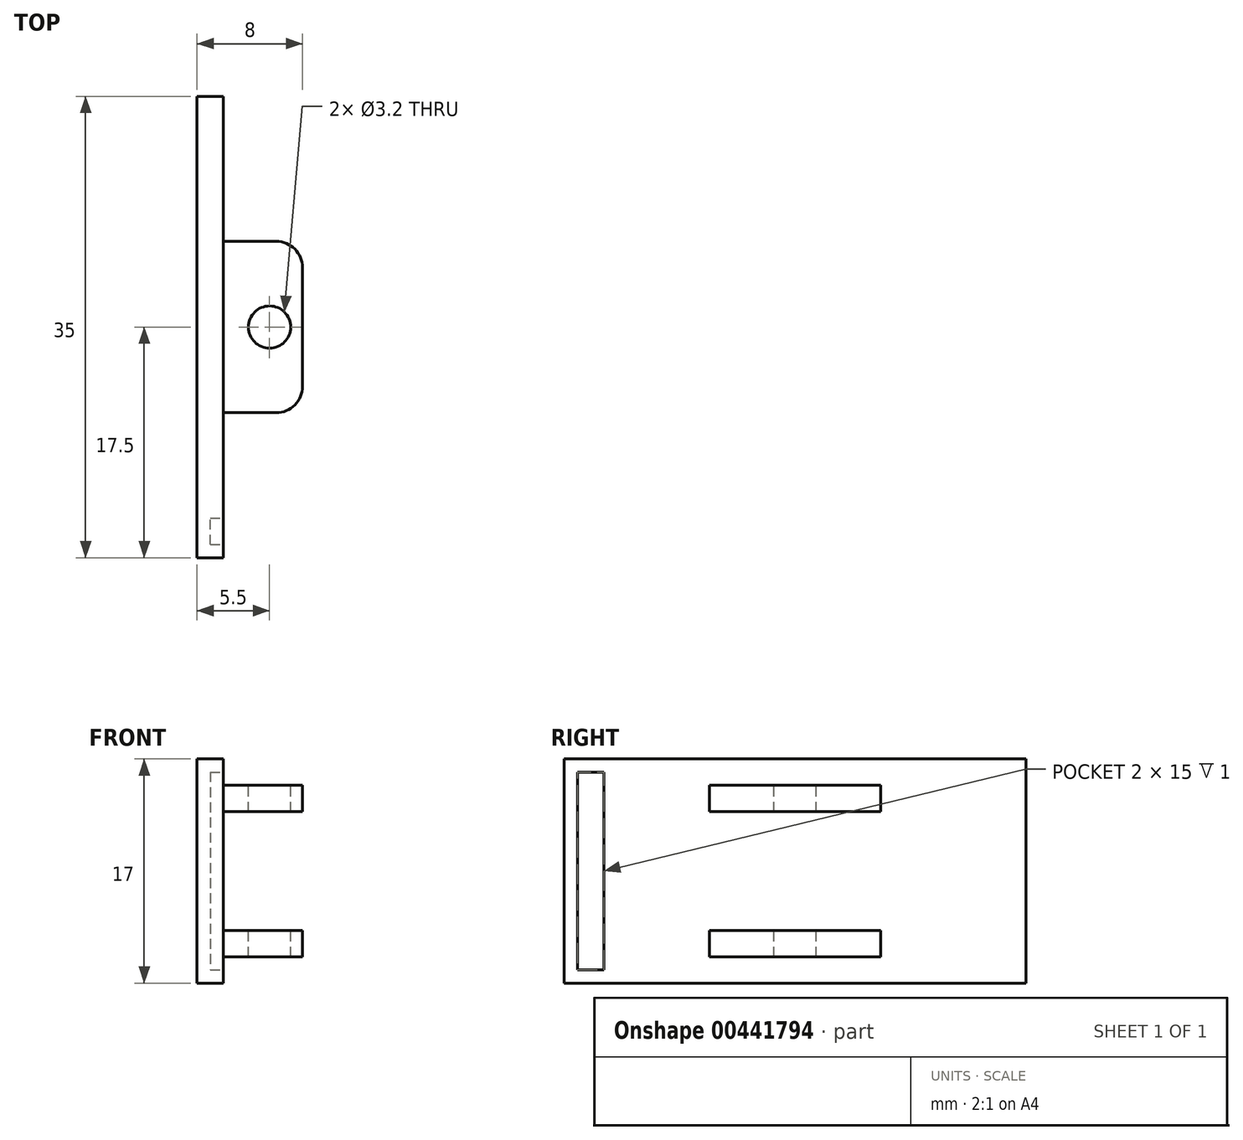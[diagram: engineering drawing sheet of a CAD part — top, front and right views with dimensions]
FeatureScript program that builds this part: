
annotation { "Feature Type Name" : "Feature", "Feature Type Description" : "" }
export const myFeature = defineFeature(function(context is Context, id is Id, definition is map)
    precondition{}
    {
        {
            var Q0;
            Q0=qCreatedBy(makeId("Right.planeOp"),FACE);
            var sketch = newSketch(context, id + "F0", { "sketchPlane" : qUnion([Q0])});
            skLineSegment(sketch, "E0.bottom", {"start": v(17.5, -8.5) * mm, "end": v(-17.5, -8.5) * mm});
            skLineSegment(sketch, "E0.top", {"start": v(17.5, 8.5) * mm, "end": v(-17.5, 8.5) * mm});
            skLineSegment(sketch, "E0.left", {"start": v(17.5, -8.5) * mm, "end": v(17.5, 8.5) * mm});
            skLineSegment(sketch, "E0.right", {"start": v(-17.5, -8.5) * mm, "end": v(-17.5, 8.5) * mm});
            skPoint(sketch, "E0.middle", {"position": v(0, 0) * mm});
            skSolve(sketch);
        }
        {
            var Q0;
            Q0=qSketchRegion(id+"F0",true);
            extrude(context, id + "F1", {"entities" : qUnion([Q0]), "depth" : 2 * mm});
        }
        {
            var Q0;
            Q0=makeQuery(id+"F1.opExtrude","CAP_FACE",FACE,{"disambiguationData":[OSD([sQuery(id+"F0.wireOp",EDGE,"E0.bottom"),sQuery(id+"F0.wireOp",EDGE,"E0.top"),sQuery(id+"F0.wireOp",EDGE,"E0.left"),sQuery(id+"F0.wireOp",EDGE,"E0.right")])],"isStart":false});
            var sketch = newSketch(context, id + "F2", { "sketchPlane" : qUnion([Q0])});
            skLineSegment(sketch, "E1.bottom", {"start": v(-16.5, 7.5) * mm, "end": v(-14.5, 7.5) * mm});
            skLineSegment(sketch, "E1.top", {"start": v(-16.5, -7.5) * mm, "end": v(-14.5, -7.5) * mm});
            skLineSegment(sketch, "E1.left", {"start": v(-16.5, 7.5) * mm, "end": v(-16.5, -7.5) * mm});
            skLineSegment(sketch, "E1.right", {"start": v(-14.5, 7.5) * mm, "end": v(-14.5, -7.5) * mm});
            skLineSegment(sketch, "E2.bottom", {"start": v(-17.5, 6.5) * mm, "end": v(15.5, 6.5) * mm});
            skLineSegment(sketch, "E2.top", {"start": v(-17.5, -6.5) * mm, "end": v(15.5, -6.5) * mm});
            skLineSegment(sketch, "E2.left", {"start": v(-17.5, 6.5) * mm, "end": v(-17.5, -6.5) * mm});
            skLineSegment(sketch, "E2.right", {"start": v(15.5, 6.5) * mm, "end": v(15.5, -6.5) * mm});
            skSolve(sketch);
        }
        {
            var Q0;
            {var subQ0=sQuery(id+"F2.wireOp",EDGE,"E2.bottom");var subQ1=sQuery(id+"F2.wireOp",EDGE,"E1.left");var subQ2=makeQuery(id+"F2.imprint","INTERSECT",VERTEX,{"derivedFrom":[subQ1,subQ0]});Q0=makeQuery(id+"F2.imprint","IMPRINT",FACE,{"disambiguationData":[TD([[makeQuery(id+"F2.imprint","IMPRINT",EDGE,{"disambiguationData":[TD([[subQ2,-1.0]])],"derivedFrom":subQ1}),1.0]])]});}
            var Q1;
            {var subQ0=sQuery(id+"F2.wireOp",EDGE,"E1.bottom");Q1=makeQuery(id+"F2.imprint","IMPRINT",FACE,{"disambiguationData":[TD([[makeQuery(id+"F2.imprint","IMPRINT",EDGE,{"derivedFrom":subQ0}),-1.0]])]});}
            var Q2;
            {var subQ0=sQuery(id+"F2.wireOp",EDGE,"E1.top");Q2=makeQuery(id+"F2.imprint","IMPRINT",FACE,{"disambiguationData":[TD([[makeQuery(id+"F2.imprint","IMPRINT",EDGE,{"derivedFrom":subQ0}),1.0]])]});}
            extrude(context, id + "F3", {"entities" : qUnion([Q0, Q1, Q2]), "operationType" : NewBodyOperationType.REMOVE, "oppositeDirection" : true, "depth" : 1 * mm});
        }
        {
            var Q0;
            Q0=makeQuery(id+"F1.opExtrude","CAP_FACE",FACE,{"disambiguationData":[OSD([sQuery(id+"F0.wireOp",EDGE,"E0.bottom"),sQuery(id+"F0.wireOp",EDGE,"E0.top"),sQuery(id+"F0.wireOp",EDGE,"E0.left"),sQuery(id+"F0.wireOp",EDGE,"E0.right")])],"isStart":false});
            var sketch = newSketch(context, id + "F4", { "sketchPlane" : qUnion([Q0])});
            skLineSegment(sketch, "E3.bottom", {"start": v(-6.5, 6.5) * mm, "end": v(6.5, 6.5) * mm});
            skLineSegment(sketch, "E3.top", {"start": v(-6.5, 4.5) * mm, "end": v(6.5, 4.5) * mm});
            skLineSegment(sketch, "E3.left", {"start": v(-6.5, 6.5) * mm, "end": v(-6.5, 4.5) * mm});
            skLineSegment(sketch, "E3.right", {"start": v(6.5, 6.5) * mm, "end": v(6.5, 4.5) * mm});
            skLineSegment(sketch, "E4.MirrorCS", {"start": v(-6.5, -4.5) * mm, "end": v(6.5, -4.5) * mm});
            skLineSegment(sketch, "E5.MirrorCS", {"start": v(-6.5, -6.5) * mm, "end": v(6.5, -6.5) * mm});
            skLineSegment(sketch, "E6.MirrorCS", {"start": v(-6.5, -6.5) * mm, "end": v(-6.5, -4.5) * mm});
            skLineSegment(sketch, "E7.MirrorCS", {"start": v(6.5, -6.5) * mm, "end": v(6.5, -4.5) * mm});
            skSolve(sketch);
        }
        {
            var Q0;
            Q0=makeQuery(id+"F4.imprint","IMPRINT",FACE,{"disambiguationData":[TD([[makeQuery(id+"F4.imprint","IMPRINT",EDGE,{"derivedFrom":sQuery(id+"F4.wireOp",EDGE,"E3.bottom")}),-1.0]])]});
            var Q1;
            Q1=makeQuery(id+"F4.imprint","IMPRINT",FACE,{"disambiguationData":[TD([[makeQuery(id+"F4.imprint","IMPRINT",EDGE,{"derivedFrom":sQuery(id+"F4.wireOp",EDGE,"E4.MirrorCS")}),-1.0]])]});
            extrude(context, id + "F5", {"entities" : qUnion([Q0, Q1]), "operationType" : NewBodyOperationType.ADD, "depth" : 6 * mm});
        }
        {
            var Q0;
            Q0=makeQuery(id+"F5.opExtrude","SWEPT_FACE",FACE,{"disambiguationData":[OSD([sQuery(id+"F4.wireOp",EDGE,"E3.bottom")])]});
            var sketch = newSketch(context, id + "F6", { "sketchPlane" : qUnion([Q0])});
            skPoint(sketch, "E8", {"position": v(5.5, 0) * mm});
            skSolve(sketch);
        }
        {
            var Q0;
            Q0=sQuery(id+"F6.wireOp",VERTEX,"E8");
            var Q1;
            Q1=makeQuery(id+"F1.opExtrude","SWEPT_BODY",BODY,{"disambiguationData":[OSD([sQuery(id+"F0.wireOp",EDGE,"E0.bottom"),sQuery(id+"F0.wireOp",EDGE,"E0.top"),sQuery(id+"F0.wireOp",EDGE,"E0.left"),sQuery(id+"F0.wireOp",EDGE,"E0.right")])]});
            hole(context, id + "F7", {"style" : HoleStyle.SIMPLE, "endStyle" : HoleEndStyle.THROUGH, "holeDiameter" : 3.2 * mm, "isTappedThrough" : true, "tappedDepth" : 12 * mm, "tapClearance" : 3, "startFromSketch" : true, "locations" : qUnion([Q0]), "scope" : qUnion([Q1])});
        }
        {
            var Q0;
            Q0=makeQuery(id+"F5.opExtrude","CAP_EDGE",EDGE,{"disambiguationData":[OSD([sQuery(id+"F4.wireOp",EDGE,"E3.right")])],"isStart":true});
            var Q1;
            Q1=makeQuery(id+"F5.opExtrude","CAP_EDGE",EDGE,{"disambiguationData":[OSD([sQuery(id+"F4.wireOp",EDGE,"E3.right")])],"isStart":false});
            var Q2;
            Q2=makeQuery(id+"F5.opExtrude","CAP_EDGE",EDGE,{"disambiguationData":[OSD([sQuery(id+"F4.wireOp",EDGE,"E7.MirrorCS")])],"isStart":false});
            var Q3;
            Q3=makeQuery(id+"F5.opExtrude","CAP_EDGE",EDGE,{"disambiguationData":[OSD([sQuery(id+"F4.wireOp",EDGE,"E7.MirrorCS")])],"isStart":true});
            var Q4;
            Q4=makeQuery(id+"F5.opExtrude","CAP_EDGE",EDGE,{"disambiguationData":[OSD([sQuery(id+"F4.wireOp",EDGE,"E6.MirrorCS")])],"isStart":true});
            var Q5;
            Q5=makeQuery(id+"F5.opExtrude","CAP_EDGE",EDGE,{"disambiguationData":[OSD([sQuery(id+"F4.wireOp",EDGE,"E6.MirrorCS")])],"isStart":false});
            var Q6;
            Q6=makeQuery(id+"F5.opExtrude","CAP_EDGE",EDGE,{"disambiguationData":[OSD([sQuery(id+"F4.wireOp",EDGE,"E3.left")])],"isStart":true});
            var Q7;
            Q7=makeQuery(id+"F5.opExtrude","CAP_EDGE",EDGE,{"disambiguationData":[OSD([sQuery(id+"F4.wireOp",EDGE,"E3.left")])],"isStart":false});
            fillet(context, id + "F8", {"entities" : qUnion([Q0, Q1, Q2, Q3, Q4, Q5, Q6, Q7]), "radius" : 2 * mm, "tangentPropagation" : true, "allowEdgeOverflow" : false});
        }
    });
